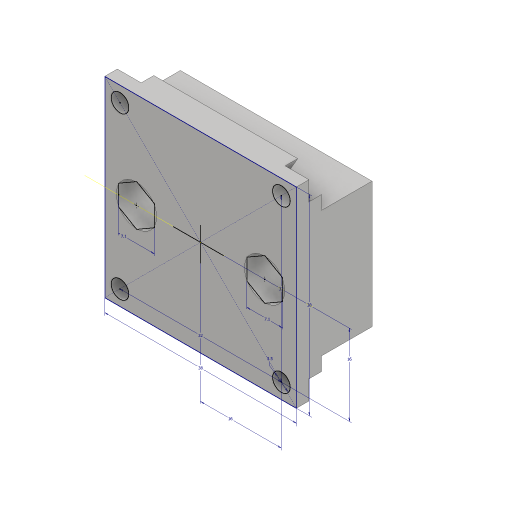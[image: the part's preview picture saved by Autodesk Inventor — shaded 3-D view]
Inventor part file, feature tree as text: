
AUTODESK INVENTOR PART (.ipt)
format: ipt  version: 2023 (Build 270158000, 158)  size: 200,192 bytes
history: native  units: mm
features: sketch x4, extrude x4, hole x2
ambient origin geometry x8: Origin, YZ Plane, XZ Plane, XY Plane, X Axis, Y Axis, Z Axis, Center Point
bodies: Body1 (feature_tree)
feature tree (10):
  sketch  "Sketch5"  dims[d47=3.5mm d48=20.0mm d50=32.0mm d51=20.0mm d53=32.0mm]
  extrude  "Extrusion3"  Depth=32.0mm
  extrude  "Extrusion4"  Depth=16.0mm
  hole  "Hole4"  [1 undecoded]
  extrude  "Extrusion6"  Depth=6.0mm
  extrude  "Extrusion7"  Depth=32.0mm
  hole  "Hole5"  [1 undecoded]
  sketch  "Sketch6"  dims[d56=16.0mm d57=16.0mm]
  sketch  "Sketch7"  dims[d58=38.0mm d59=38.0mm]
  sketch  "Sketch8"  dims[d60=5.0mm d61=0.0mm d62=6.0mm d63=20.0mm d65=32.0mm d66=20.0mm d68=32.0mm d71=2.5mm d72=0.0mm d73=7.1mm d74=7.1mm d77=4.2mm d78=6.0mm d79=4.0mm d80=2.0mm d81=90.0deg d82=8.0mm d83=20.594885mm d84=2.5mm d85=0.0mm d86=25.0mm d87=10.0mm d88=0.0mm d89=8.0mm d90=3.4mm d91=3.023mm d92=2.0mm d93=14.3117mm d94=8.0mm d95=0.0mm]
note: 2 required parameter values undecoded (feature->parameter linkage not recoverable at this tier; creation-order binding heuristic only, values carry confidence <= 0.55)
